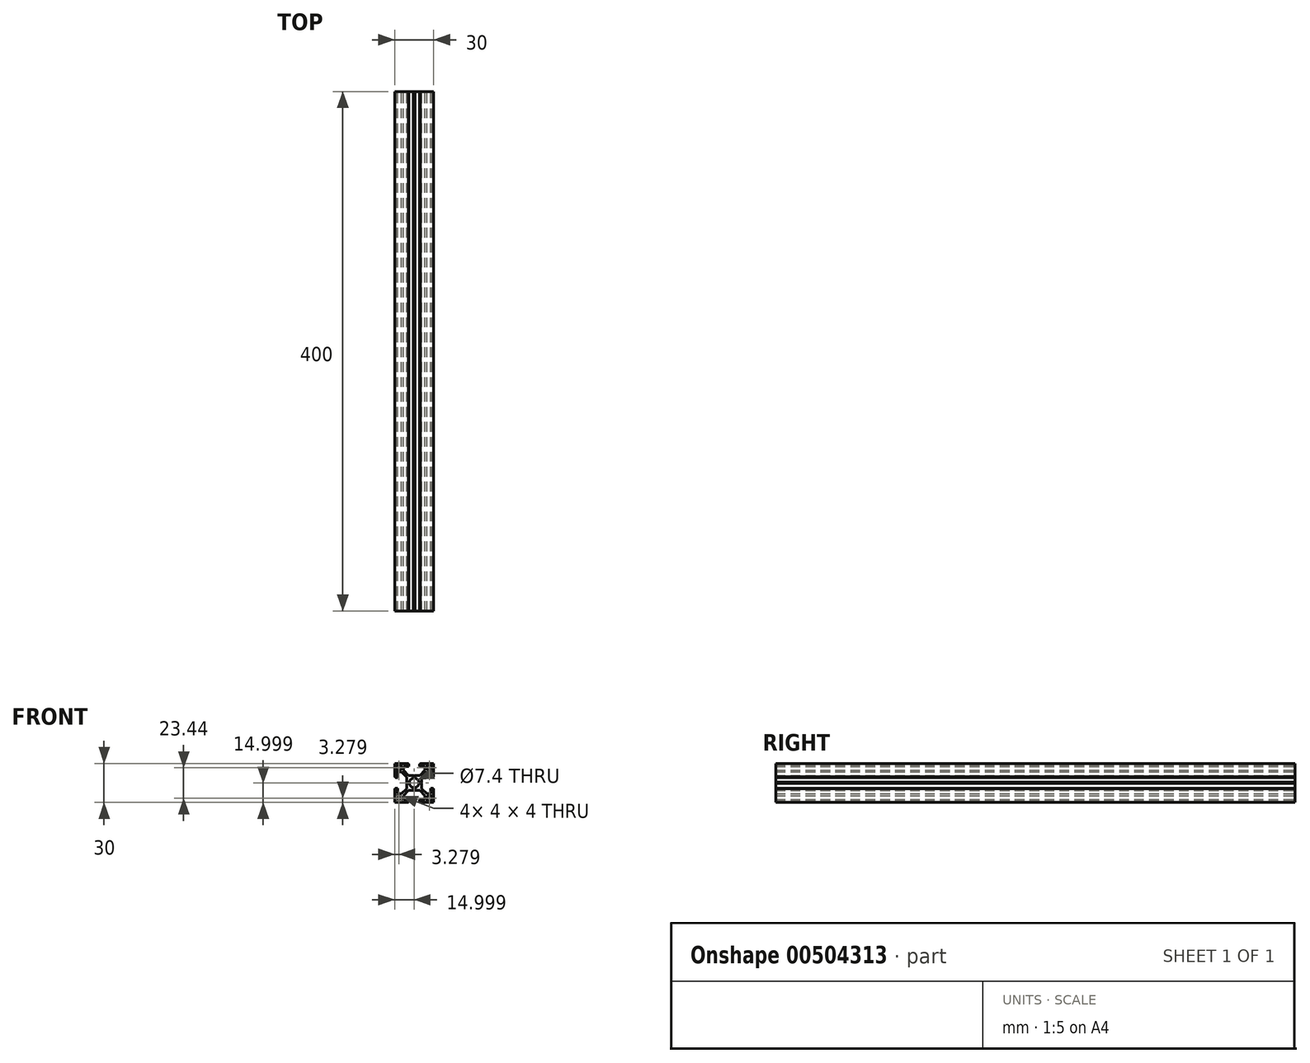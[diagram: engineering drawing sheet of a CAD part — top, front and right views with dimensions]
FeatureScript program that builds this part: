
annotation { "Feature Type Name" : "Feature", "Feature Type Description" : "" }
export const myFeature = defineFeature(function(context is Context, id is Id, definition is map)
    precondition{}
    {
        {
            var Q0;
            Q0=qCreatedBy(makeId("Front.planeOp"),FACE);
            var sketch = newSketch(context, id + "F0", { "sketchPlane" : qUnion([Q0])});
            skLineSegment(sketch, "E0", {"start": v(-14.5, 14.82) * mm, "end": v(-4.1, 14.82) * mm});
            skLineSegment(sketch, "E1", {"start": v(-4.1, 14.82) * mm, "end": v(-4.1, 14.32) * mm});
            skLineSegment(sketch, "E2", {"start": v(-4.1, 14.32) * mm, "end": v(-3.6, 14.32) * mm});
            skLineSegment(sketch, "E3", {"start": v(-3.6, 14.32) * mm, "end": v(-3.6, 12.62) * mm});
            skLineSegment(sketch, "E4", {"start": v(-3.6, 12.62) * mm, "end": v(-7.9, 12.62) * mm});
            skLineSegment(sketch, "E5", {"start": v(-7.9, 12.62) * mm, "end": v(-7.9, 9.62) * mm});
            skLineSegment(sketch, "E6", {"start": v(-7.9, 9.62) * mm, "end": v(-3.85, 5.57) * mm});
            skLineSegment(sketch, "E7", {"start": v(-3.85, 5.57) * mm, "end": v(0, 5.57) * mm});
            skLineSegment(sketch, "E8", {"start": v(0, 5.57) * mm, "end": v(0.5, 5.07) * mm});
            skLineSegment(sketch, "E9", {"start": v(0.5, 5.07) * mm, "end": v(1, 5.57) * mm});
            skLineSegment(sketch, "E10", {"start": v(1, 5.57) * mm, "end": v(4.85, 5.57) * mm});
            skLineSegment(sketch, "E11", {"start": v(4.85, 5.57) * mm, "end": v(8.9, 9.62) * mm});
            skLineSegment(sketch, "E12", {"start": v(8.9, 9.62) * mm, "end": v(8.9, 12.62) * mm});
            skLineSegment(sketch, "E13", {"start": v(8.9, 12.62) * mm, "end": v(4.6, 12.62) * mm});
            skLineSegment(sketch, "E14", {"start": v(4.6, 12.62) * mm, "end": v(4.6, 14.32) * mm});
            skLineSegment(sketch, "E15", {"start": v(4.6, 14.32) * mm, "end": v(5.1, 14.32) * mm});
            skLineSegment(sketch, "E16", {"start": v(5.1, 14.32) * mm, "end": v(5.1, 14.82) * mm});
            skLineSegment(sketch, "E17", {"start": v(5.1, 14.82) * mm, "end": v(15.5, 14.82) * mm});
            skLineSegment(sketch, "E18", {"start": v(15.5, 14.82) * mm, "end": v(15.5, 4.42) * mm});
            skLineSegment(sketch, "E19", {"start": v(15.5, 4.42) * mm, "end": v(15, 4.42) * mm});
            skLineSegment(sketch, "E20", {"start": v(15, 4.42) * mm, "end": v(15, 3.92) * mm});
            skLineSegment(sketch, "E21", {"start": v(15, 3.92) * mm, "end": v(13.3, 3.92) * mm});
            skLineSegment(sketch, "E22", {"start": v(13.3, 3.92) * mm, "end": v(13.3, 8.22) * mm});
            skLineSegment(sketch, "E23", {"start": v(13.3, 8.22) * mm, "end": v(10.3, 8.22) * mm});
            skLineSegment(sketch, "E24", {"start": v(10.3, 8.22) * mm, "end": v(6.26, 4.17) * mm});
            skLineSegment(sketch, "E25", {"start": v(6.26, 4.17) * mm, "end": v(6.26, 0.32) * mm});
            skLineSegment(sketch, "E26", {"start": v(5.76, -0.18) * mm, "end": v(6.26, 0.32) * mm});
            skLineSegment(sketch, "E27", {"start": v(6.26, -0.68) * mm, "end": v(5.76, -0.18) * mm});
            skLineSegment(sketch, "E28", {"start": v(6.26, -0.68) * mm, "end": v(6.26, -4.53) * mm});
            skLineSegment(sketch, "E29", {"start": v(6.26, -4.53) * mm, "end": v(10.3, -8.58) * mm});
            skLineSegment(sketch, "E30", {"start": v(10.3, -8.58) * mm, "end": v(13.3, -8.58) * mm});
            skLineSegment(sketch, "E31", {"start": v(13.3, -8.58) * mm, "end": v(13.3, -4.28) * mm});
            skLineSegment(sketch, "E32", {"start": v(13.3, -4.28) * mm, "end": v(15, -4.28) * mm});
            skLineSegment(sketch, "E33", {"start": v(15, -4.28) * mm, "end": v(15, -4.78) * mm});
            skLineSegment(sketch, "E34", {"start": v(15, -4.78) * mm, "end": v(15.5, -4.78) * mm});
            skLineSegment(sketch, "E35", {"start": v(15.5, -4.78) * mm, "end": v(15.5, -15.18) * mm});
            skLineSegment(sketch, "E36", {"start": v(15.5, -15.18) * mm, "end": v(5.1, -15.18) * mm});
            skLineSegment(sketch, "E37", {"start": v(5.1, -15.18) * mm, "end": v(5.1, -14.68) * mm});
            skLineSegment(sketch, "E38", {"start": v(5.1, -14.68) * mm, "end": v(4.6, -14.68) * mm});
            skLineSegment(sketch, "E39", {"start": v(4.6, -14.68) * mm, "end": v(4.6, -12.98) * mm});
            skLineSegment(sketch, "E40", {"start": v(4.6, -12.98) * mm, "end": v(8.9, -12.98) * mm});
            skLineSegment(sketch, "E41", {"start": v(8.9, -12.98) * mm, "end": v(8.9, -9.98) * mm});
            skLineSegment(sketch, "E42", {"start": v(8.9, -9.98) * mm, "end": v(4.86, -5.93) * mm});
            skLineSegment(sketch, "E43", {"start": v(4.86, -5.93) * mm, "end": v(1, -5.93) * mm});
            skLineSegment(sketch, "E44", {"start": v(1, -5.93) * mm, "end": v(0.5, -5.43) * mm});
            skLineSegment(sketch, "E45", {"start": v(0.5, -5.43) * mm, "end": v(0, -5.93) * mm});
            skLineSegment(sketch, "E46", {"start": v(0, -5.93) * mm, "end": v(-3.84, -5.93) * mm});
            skLineSegment(sketch, "E47", {"start": v(-3.84, -5.93) * mm, "end": v(-7.9, -9.98) * mm});
            skLineSegment(sketch, "E48", {"start": v(-7.9, -9.98) * mm, "end": v(-7.9, -12.98) * mm});
            skLineSegment(sketch, "E49", {"start": v(-7.9, -12.98) * mm, "end": v(-3.6, -12.98) * mm});
            skLineSegment(sketch, "E50", {"start": v(-3.6, -12.98) * mm, "end": v(-3.6, -14.68) * mm});
            skLineSegment(sketch, "E51", {"start": v(-3.6, -14.68) * mm, "end": v(-4.1, -14.68) * mm});
            skLineSegment(sketch, "E52", {"start": v(-4.1, -14.68) * mm, "end": v(-4.1, -15.18) * mm});
            skLineSegment(sketch, "E53", {"start": v(-4.1, -15.18) * mm, "end": v(-14.5, -15.18) * mm});
            skLineSegment(sketch, "E54", {"start": v(-14.5, -15.18) * mm, "end": v(-14.5, -4.78) * mm});
            skLineSegment(sketch, "E55", {"start": v(-14.5, -4.78) * mm, "end": v(-14, -4.78) * mm});
            skLineSegment(sketch, "E56", {"start": v(-14, -4.78) * mm, "end": v(-14, -4.28) * mm});
            skLineSegment(sketch, "E57", {"start": v(-14, -4.28) * mm, "end": v(-12.3, -4.28) * mm});
            skLineSegment(sketch, "E58", {"start": v(-12.3, -4.28) * mm, "end": v(-12.3, -8.58) * mm});
            skLineSegment(sketch, "E59", {"start": v(-12.3, -8.58) * mm, "end": v(-9.3, -8.58) * mm});
            skLineSegment(sketch, "E60", {"start": v(-9.3, -8.58) * mm, "end": v(-5.24, -4.53) * mm});
            skLineSegment(sketch, "E61", {"start": v(-5.24, -4.53) * mm, "end": v(-5.24, -0.68) * mm});
            skLineSegment(sketch, "E62", {"start": v(-5.24, -0.68) * mm, "end": v(-4.74, -0.18) * mm});
            skLineSegment(sketch, "E63", {"start": v(-4.74, -0.18) * mm, "end": v(-5.24, 0.32) * mm});
            skLineSegment(sketch, "E64", {"start": v(-5.24, 0.32) * mm, "end": v(-5.24, 4.17) * mm});
            skLineSegment(sketch, "E65", {"start": v(-5.24, 4.17) * mm, "end": v(-9.3, 8.22) * mm});
            skLineSegment(sketch, "E66", {"start": v(-9.3, 8.22) * mm, "end": v(-12.3, 8.22) * mm});
            skLineSegment(sketch, "E67", {"start": v(-12.3, 8.22) * mm, "end": v(-12.3, 3.92) * mm});
            skLineSegment(sketch, "E68", {"start": v(-12.3, 3.92) * mm, "end": v(-14, 3.92) * mm});
            skLineSegment(sketch, "E69", {"start": v(-14, 3.92) * mm, "end": v(-14, 4.42) * mm});
            skLineSegment(sketch, "E70", {"start": v(-14, 4.42) * mm, "end": v(-14.5, 4.42) * mm});
            skLineSegment(sketch, "E71", {"start": v(-14.5, 4.42) * mm, "end": v(-14.5, 14.82) * mm});
            skSolve(sketch);
        }
        {
            var Q0;
            Q0=qCreatedBy(makeId("Front.planeOp"),FACE);
            var sketch = newSketch(context, id + "F1", { "sketchPlane" : qUnion([Q0])});
            skCircle(sketch, "E72", {"center": v(0.5, -0.18) * mm, "radius": 3.7 * mm});
            skLineSegment(sketch, "E73.bottom", {"start": v(10.23, 13.54) * mm, "end": v(14.23, 13.54) * mm});
            skLineSegment(sketch, "E73.top", {"start": v(10.23, 9.54) * mm, "end": v(14.23, 9.54) * mm});
            skLineSegment(sketch, "E73.left", {"start": v(10.23, 13.54) * mm, "end": v(10.23, 9.54) * mm});
            skLineSegment(sketch, "E73.right", {"start": v(14.23, 13.54) * mm, "end": v(14.23, 9.54) * mm});
            skLineSegment(sketch, "E74.bottom", {"start": v(10.23, -9.9) * mm, "end": v(14.23, -9.9) * mm});
            skLineSegment(sketch, "E74.top", {"start": v(10.23, -13.9) * mm, "end": v(14.23, -13.9) * mm});
            skLineSegment(sketch, "E74.left", {"start": v(10.23, -9.9) * mm, "end": v(10.23, -13.9) * mm});
            skLineSegment(sketch, "E74.right", {"start": v(14.23, -9.9) * mm, "end": v(14.23, -13.9) * mm});
            skLineSegment(sketch, "E75.bottom", {"start": v(-13.21, -9.9) * mm, "end": v(-9.21, -9.9) * mm});
            skLineSegment(sketch, "E75.top", {"start": v(-13.21, -13.9) * mm, "end": v(-9.21, -13.9) * mm});
            skLineSegment(sketch, "E75.left", {"start": v(-13.21, -9.9) * mm, "end": v(-13.21, -13.9) * mm});
            skLineSegment(sketch, "E75.right", {"start": v(-9.21, -9.9) * mm, "end": v(-9.21, -13.9) * mm});
            skLineSegment(sketch, "E76.bottom", {"start": v(-13.21, 13.54) * mm, "end": v(-9.21, 13.54) * mm});
            skLineSegment(sketch, "E76.top", {"start": v(-13.21, 9.54) * mm, "end": v(-9.21, 9.54) * mm});
            skLineSegment(sketch, "E76.left", {"start": v(-13.21, 13.54) * mm, "end": v(-13.21, 9.54) * mm});
            skLineSegment(sketch, "E76.right", {"start": v(-9.21, 13.54) * mm, "end": v(-9.21, 9.54) * mm});
            skSolve(sketch);
        }
        {
            var Q0;
            Q0 = qSketchRegion(id + "F0", true);
            extrude(context, id + "F2", {"entities" : qUnion([Q0]), "depth" : 400 * mm, "offsetDistance" : 25 * mm});
        }
        {
            var Q0;
            Q0 = qSketchRegion(id + "F1", true);
            extrude(context, id + "F3", {"entities" : qUnion([Q0]), "operationType" : NewBodyOperationType.REMOVE, "endBound" : BoundingType.THROUGH_ALL, "depth" : 25 * mm, "offsetDistance" : 25 * mm});
        }
    });
